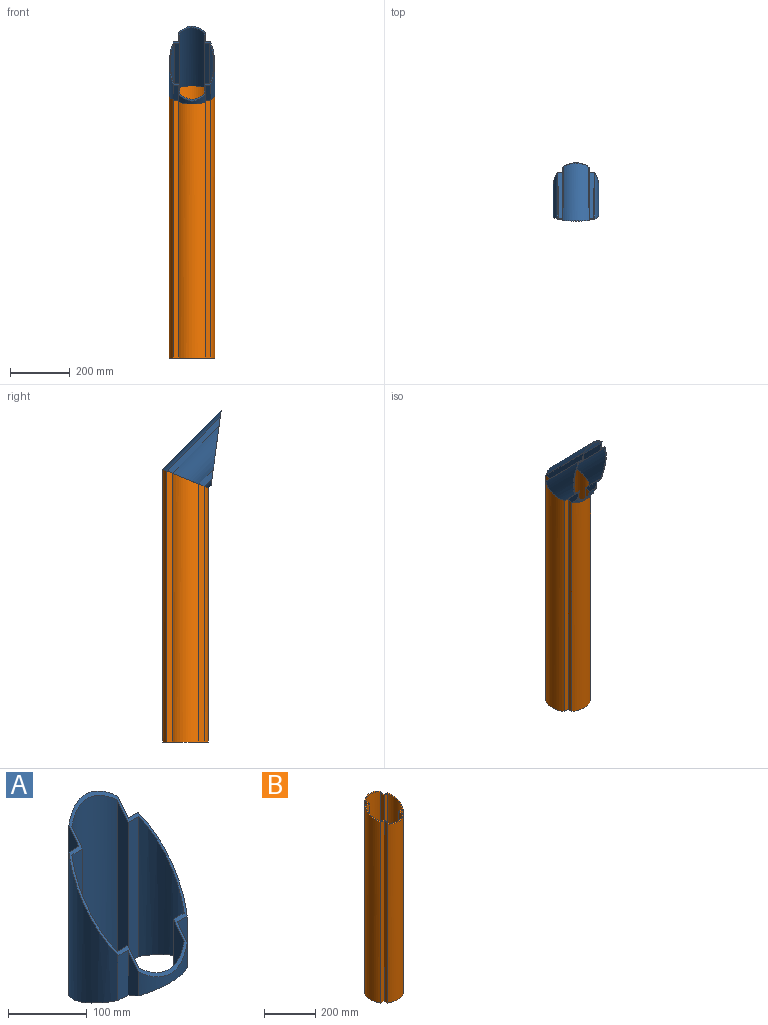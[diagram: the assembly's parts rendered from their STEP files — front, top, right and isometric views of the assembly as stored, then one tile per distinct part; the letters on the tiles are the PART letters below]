
ASSEMBLY  parts=2 mates=1
PART A: 26 faces, bbox 152.4x152.4x279.5 mm
  f0: cylinder r=76.2mm len=223.51mm, axis (0,0,-1), area 13800.9mm2, adj f1,f11,f12,f13
  f1: plane 69.74x18mm, normal (0,-1,0), area 1255.1mm2, adj f0,f2,f12,f13
  f2: plane 69.74x18mm, normal (1,0,0), area 972.9mm2, adj f1,f3,f12,f13
  f3: cylinder r=76.2mm len=88.25mm, axis (0,0,-1), area 2083.2mm2, adj f2,f4,f12,f13
  f4: plane 69.74x18mm, normal (-1,0,0), area 972.9mm2, adj f3,f5,f12,f13
  f5: plane 69.74x18mm, normal (0,-1,0), area 1255.1mm2, adj f4,f6,f12,f13
  f6: cylinder r=76.2mm len=223.34mm, axis (0,0,-1), area 13773.1mm2, adj f5,f7,f12,f13
  f7: plane 223.39x18mm, normal (0,1,0), area 4019.9mm2, adj f6,f8,f12,f13
  f8: plane 254.75x18mm, normal (-1,0,0), area 4302.5mm2, adj f7,f9,f12,f13
  f9: cylinder r=76.2mm len=279.47mm, axis (0,0,-1), area 25550.2mm2, adj f8,f10,f12,f13
  f10: plane 254.87x18mm, normal (1,0,0), area 4304.8mm2, adj f9,f11,f12,f13
  f11: plane 223.51x18mm, normal (0,1,0), area 4022.6mm2, adj f0,f10,f12,f13
  f12: plane 152.4x152.4mm, normal (0,-0.38,-0.93), area 1900.2mm2, adj f0,f1,f2,f3,f4,f5,f6,f7
  f13: plane 203.2x152.4mm, normal (0,-0.8,0.6), area 2931.3mm2, adj f0,f1,f2,f3,f4,f5,f6,f7
  f14: cylinder r=72.64mm len=217.98mm, axis (0,0,-1), area 12758.1mm2, adj f12,f13,f15,f25
  f15: plane 75.27x19.05mm, normal (0,1,0), area 1433.9mm2, adj f12,f13,f14,f16
  f16: plane 75.27x19.05mm, normal (-1,0,0), area 1117.7mm2, adj f12,f13,f15,f17
  f17: cylinder r=72.64mm len=81.9mm, axis (0,0,-1), area 2391mm2, adj f12,f13,f16,f18
  f18: plane 75.27x19.05mm, normal (1,0,0), area 1117.7mm2, adj f12,f13,f17,f19
  f19: plane 75.27x19.05mm, normal (0,1,0), area 1433.9mm2, adj f12,f13,f18,f20
  f20: cylinder r=72.64mm len=217.81mm, axis (0,0,-1), area 12732.3mm2, adj f12,f13,f19,f21
  f21: plane 217.86x19.05mm, normal (0,-1,0), area 4149.8mm2, adj f12,f13,f20,f22
  f22: plane 251.06x19.05mm, normal (1,0,0), area 4466.5mm2, adj f12,f13,f21,f23
  f23: cylinder r=72.64mm len=273.27mm, axis (0,0,-1), area 23154.9mm2, adj f12,f13,f22,f24
  f24: plane 251.17x19.05mm, normal (-1,0,0), area 4468.7mm2, adj f12,f13,f23,f25
  f25: plane 217.98x19.05mm, normal (0,-1,0), area 4152.5mm2, adj f12,f13,f14,f24
PART B: 26 faces, bbox 152.4x152.4x914.4 mm
  f0: plane 901.28x18mm, normal (0,1,0), area 16220.5mm2, adj f1,f23,f24,f25
  f1: plane 908.64x18mm, normal (1,0,0), area 16286.7mm2, adj f0,f2,f24,f25
  f2: cylinder r=76.2mm len=914.42mm, axis (0,0,-1), area 85789.6mm2, adj f1,f3,f24,f25
  f3: plane 908.67x18mm, normal (-1,0,0), area 16287.1mm2, adj f2,f4,f24,f25
  f4: plane 901.31x18mm, normal (0,1,0), area 16221mm2, adj f3,f5,f24,f25
  f5: cylinder r=76.2mm len=901.31mm, axis (0,0,-1), area 83224.6mm2, adj f4,f6,f24,f25
  f6: plane 865.17x18mm, normal (0,-1,0), area 15570.7mm2, adj f5,f7,f24,f25
  f7: plane 865.17x18mm, normal (-1,0,0), area 15504.4mm2, adj f6,f8,f24,f25
  f8: cylinder r=76.2mm len=857.81mm, axis (0,0,-1), area 80380.7mm2, adj f7,f9,f24,f25
  f9: plane 865.17x18mm, normal (1,0,0), area 15504.4mm2, adj f8,f10,f24,f25
  f10: plane 865.17x18mm, normal (0,-1,0), area 15570.7mm2, adj f9,f23,f24,f25
  f11: cylinder r=72.64mm len=899.98mm, axis (0,0,-1), area 76850.6mm2, adj f12,f22,f24,f25
  f12: plane 866.47x19.05mm, normal (0,1,0), area 16506.3mm2, adj f11,f13,f24,f25
  f13: plane 866.47x19.05mm, normal (-1,0,0), area 16432.1mm2, adj f12,f14,f24,f25
  f14: cylinder r=72.64mm len=858.68mm, axis (0,0,-1), area 74416.6mm2, adj f13,f15,f24,f25
  f15: plane 866.47x19.05mm, normal (1,0,0), area 16432.1mm2, adj f14,f16,f24,f25
  f16: plane 866.47x19.05mm, normal (0,1,0), area 16506.3mm2, adj f15,f17,f24,f25
  f17: cylinder r=72.64mm len=900.01mm, axis (0,0,-1), area 76938.9mm2, adj f16,f18,f24,f25
  f18: plane 900.01x19.05mm, normal (0,-1,0), area 17145.1mm2, adj f17,f19,f24,f25
  f19: plane 907.8x19.05mm, normal (1,0,0), area 17219.3mm2, adj f18,f20,f24,f25
  f20: cylinder r=72.64mm len=912.96mm, axis (0,0,-1), area 79195.7mm2, adj f19,f21,f24,f25
  f21: plane 907.77x19.05mm, normal (-1,0,0), area 17218.8mm2, adj f20,f22,f24,f25
  f22: plane 899.98x19.05mm, normal (0,-1,0), area 17144.6mm2, adj f11,f21,f24,f25
  f23: cylinder r=76.2mm len=901.28mm, axis (0,0,-1), area 83131.9mm2, adj f0,f10,f24,f25
  f24: plane 152.4x152.4mm, normal (0,0,-1), area 1758.8mm2, adj f0,f1,f2,f3,f4,f5,f6,f7
  f25: plane 152.4x152.4mm, normal (0,-0.38,0.93), area 1900.2mm2, adj f0,f1,f2,f3,f4,f5,f6,f7
PLACE A rot(axis=(1,0,0),44.5deg) t=(-482.49,-29.09,745.23)mm
PLACE B t=(-482.49,-50.94,-115.77)mm
MATE fastened A.f12 <-> B.f25  axis (0,0.38,-0.93) through (-482.49,-50.94,767.46)mm
